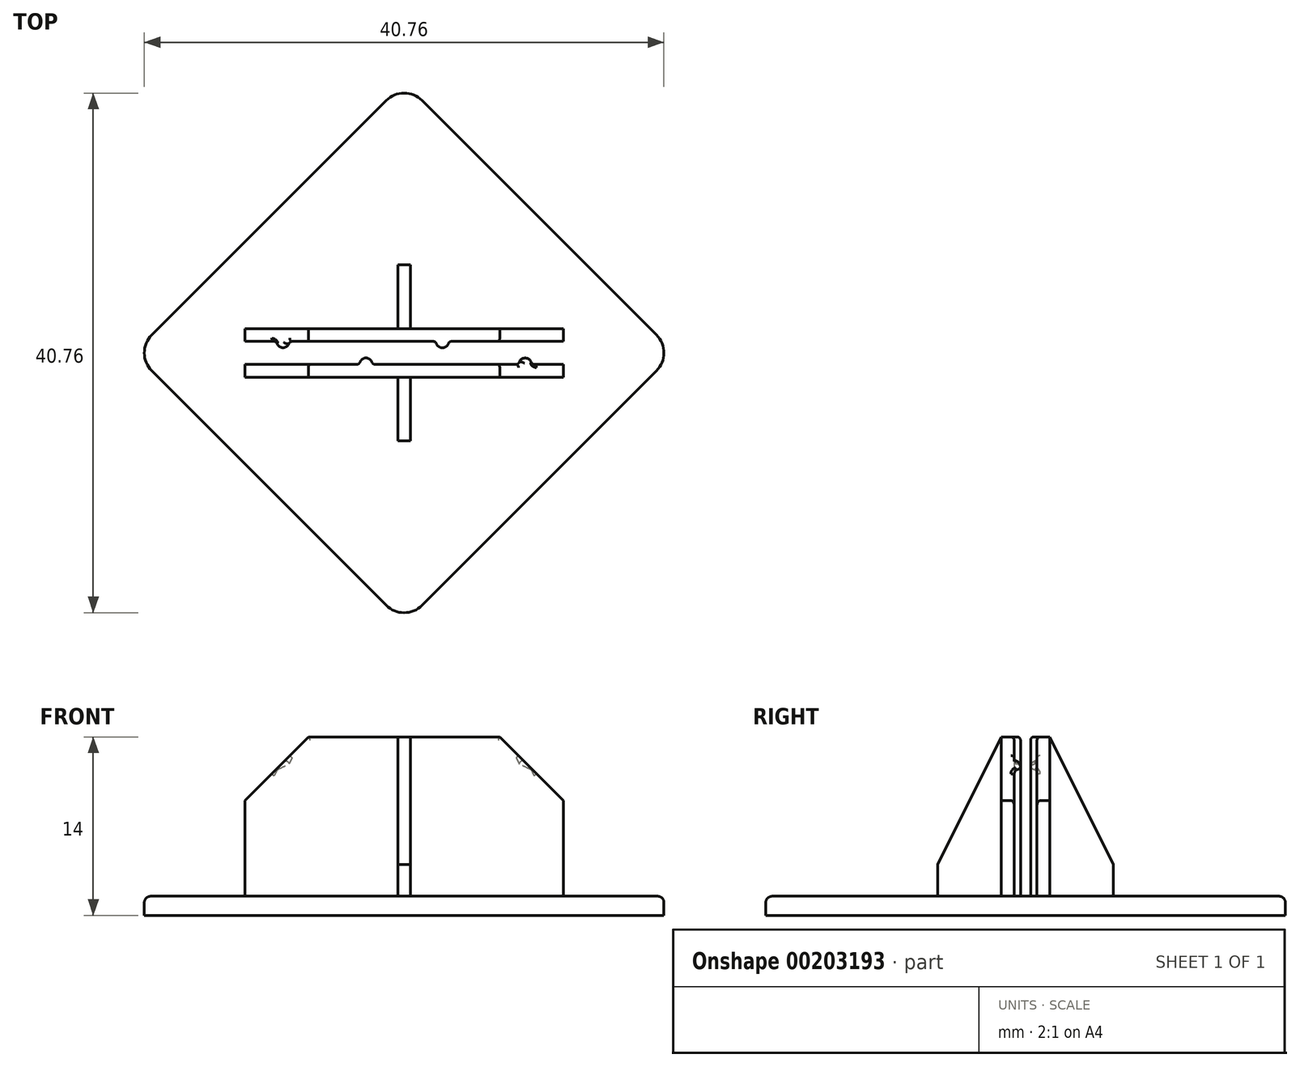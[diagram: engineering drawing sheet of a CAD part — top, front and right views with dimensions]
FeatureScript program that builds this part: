
annotation { "Feature Type Name" : "Feature", "Feature Type Description" : "" }
export const myFeature = defineFeature(function(context is Context, id is Id, definition is map)
    precondition{}
    {
        {
            var Q0;
            Q0=qCreatedBy(makeId("Front.planeOp"),FACE);
            var sketch = newSketch(context, id + "F0", { "sketchPlane" : qUnion([Q0])});
            skLineSegment(sketch, "E0", {"start": v(0, 0) * mm, "end": v(0, 22.97) * mm, "construction": true});
            skSolve(sketch);
        }
        {
            var Q0;
            Q0=qCreatedBy(makeId("Top.planeOp"),FACE);
            var sketch = newSketch(context, id + "F1", { "sketchPlane" : qUnion([Q0])});
            skLineSegment(sketch, "E1.bottom", {"start": v(15, -15) * mm, "end": v(-15, -15) * mm});
            skLineSegment(sketch, "E1.top", {"start": v(15, 15) * mm, "end": v(-15, 15) * mm});
            skLineSegment(sketch, "E1.left", {"start": v(15, -15) * mm, "end": v(15, 15) * mm});
            skLineSegment(sketch, "E1.right", {"start": v(-15, -15) * mm, "end": v(-15, 15) * mm});
            skPoint(sketch, "E1.middle", {"position": v(0, 0) * mm});
            skSolve(sketch);
        }
        {
            var Q0;
            Q0=makeQuery(id+"F1.imprint","IMPRINT",FACE,{"disambiguationData":[TD([[makeQuery(id+"F1.imprint","IMPRINT",EDGE,{"derivedFrom":sQuery(id+"F1.wireOp",EDGE,"E1.bottom")}),-1.0]])]});
            extrude(context, id + "F2", {"entities" : qUnion([Q0]), "depth" : 1.5 * mm});
        }
        {
            var Q0;
            Q0=makeQuery(id+"F2.opExtrude","SWEPT_BODY",BODY,{"disambiguationData":[OSD([sQuery(id+"F1.wireOp",EDGE,"E1.bottom"),sQuery(id+"F1.wireOp",EDGE,"E1.top"),sQuery(id+"F1.wireOp",EDGE,"E1.left"),sQuery(id+"F1.wireOp",EDGE,"E1.right")])]});
            var Q1;
            Q1=sQuery(id+"F0.wireOp",EDGE,"E0");
            transform(context, id + "F3", {"entities" : qUnion([Q0]), "transformType" : TransformType.ROTATION, "transformAxis" : qUnion([Q1]), "angle" : 45 * degree, "makeCopy" : false});
        }
        {
            var Q0;
            Q0=makeQuery(id+"F2.opExtrude","SWEPT_EDGE",EDGE,{"disambiguationData":[OSD([sQuery(id+"F1.wireOp",EDGE,"E1.top"),sQuery(id+"F1.wireOp",EDGE,"E1.right")])]});
            var Q1;
            Q1=makeQuery(id+"F2.opExtrude","SWEPT_EDGE",EDGE,{"disambiguationData":[OSD([sQuery(id+"F1.wireOp",EDGE,"E1.bottom"),sQuery(id+"F1.wireOp",EDGE,"E1.right")])]});
            var Q2;
            Q2=makeQuery(id+"F2.opExtrude","SWEPT_EDGE",EDGE,{"disambiguationData":[OSD([sQuery(id+"F1.wireOp",EDGE,"E1.bottom"),sQuery(id+"F1.wireOp",EDGE,"E1.left")])]});
            var Q3;
            Q3=makeQuery(id+"F2.opExtrude","SWEPT_EDGE",EDGE,{"disambiguationData":[OSD([sQuery(id+"F1.wireOp",EDGE,"E1.top"),sQuery(id+"F1.wireOp",EDGE,"E1.left")])]});
            fillet(context, id + "F4", {"entities" : qUnion([Q0, Q1, Q2, Q3]), "radius" : 2 * mm, "tangentPropagation" : true, "allowEdgeOverflow" : false});
        }
        {
            var Q0;
            Q0=makeQuery(id+"F2.opExtrude","CAP_FACE",FACE,{"disambiguationData":[OSD([sQuery(id+"F1.wireOp",EDGE,"E1.bottom"),sQuery(id+"F1.wireOp",EDGE,"E1.top"),sQuery(id+"F1.wireOp",EDGE,"E1.left"),sQuery(id+"F1.wireOp",EDGE,"E1.right")])],"isStart":false});
            fillet(context, id + "F5", {"entities" : qUnion([Q0]), "radius" : .5 * mm, "tangentPropagation" : true, "allowEdgeOverflow" : false});
        }
        {
            var Q0;
            Q0=makeQuery(id+"F2.opExtrude","CAP_FACE",FACE,{"disambiguationData":[OSD([sQuery(id+"F1.wireOp",EDGE,"E1.bottom"),sQuery(id+"F1.wireOp",EDGE,"E1.top"),sQuery(id+"F1.wireOp",EDGE,"E1.left"),sQuery(id+"F1.wireOp",EDGE,"E1.right")])],"isStart":false});
            var sketch = newSketch(context, id + "F6", { "sketchPlane" : qUnion([Q0])});
            skLineSegment(sketch, "E2", {"start": v(-18.38, 0) * mm, "end": v(18.38, 0) * mm, "construction": true});
            skLineSegment(sketch, "E3.0", {"start": v(-18.38, 1) * mm, "end": v(18.38, 1) * mm, "construction": true});
            skLineSegment(sketch, "E4.0", {"start": v(-18.38, 2) * mm, "end": v(18.38, 2) * mm, "construction": true});
            skLineSegment(sketch, "E5.0", {"start": v(-18.38, 7) * mm, "end": v(18.38, 7) * mm, "construction": true});
            skLineSegment(sketch, "E6", {"start": v(0, 18.38) * mm, "end": v(0, -18.38) * mm, "construction": true});
            skLineSegment(sketch, "E7.0", {"start": v(-12.5, 18.38) * mm, "end": v(-12.5, -18.38) * mm, "construction": true});
            skLineSegment(sketch, "E8.0", {"start": v(12.5, 18.38) * mm, "end": v(12.5, -18.38) * mm, "construction": true});
            skLineSegment(sketch, "E9.0", {"start": v(-0.5, 18.38) * mm, "end": v(-0.5, -18.38) * mm, "construction": true});
            skLineSegment(sketch, "E10.0", {"start": v(0.5, 18.38) * mm, "end": v(0.5, -18.38) * mm, "construction": true});
            skLineSegment(sketch, "E11.0", {"start": v(-9.5, 18.38) * mm, "end": v(-9.5, -18.38) * mm, "construction": true});
            skLineSegment(sketch, "E12.0", {"start": v(3, 18.38) * mm, "end": v(3, -18.38) * mm, "construction": true});
            skCircle(sketch, "E13", {"center": v(-9.5, 1) * mm, "radius": 0.5 * mm});
            skCircle(sketch, "E14", {"center": v(3, 1) * mm, "radius": 0.5 * mm});
            skLineSegment(sketch, "E15", {"start": v(0.5, 7) * mm, "end": v(0.5, 2) * mm});
            skLineSegment(sketch, "E16", {"start": v(0.5, 2) * mm, "end": v(12.5, 2) * mm});
            skLineSegment(sketch, "E17", {"start": v(12.5, 2) * mm, "end": v(12.5, 1) * mm});
            skLineSegment(sketch, "E18", {"start": v(12.5, 1) * mm, "end": v(-12.5, 1) * mm});
            skLineSegment(sketch, "E19", {"start": v(-12.5, 1) * mm, "end": v(-12.5, 2) * mm});
            skLineSegment(sketch, "E20", {"start": v(-12.5, 2) * mm, "end": v(-0.5, 2) * mm});
            skLineSegment(sketch, "E21", {"start": v(-0.5, 2) * mm, "end": v(-0.5, 7) * mm});
            skLineSegment(sketch, "E22", {"start": v(-0.5, 7) * mm, "end": v(0.5, 7) * mm});
            skSolve(sketch);
        }
        {
            var Q0;
            Q0=makeQuery(id+"F6.imprint","IMPRINT",FACE,{"disambiguationData":[TD([[makeQuery(id+"F6.imprint","IMPRINT",EDGE,{"derivedFrom":sQuery(id+"F6.wireOp",EDGE,"E15")}),-1.0]])]});
            var Q1;
            {var subQ0=sQuery(id+"F6.wireOp",EDGE,"E18");var subQ1=sQuery(id+"F6.wireOp",EDGE,"E13");var subQ2=makeQuery(id+"F6.imprint","INTERSECT",VERTEX,{"disambiguationData":[OD(0.0)],"derivedFrom":[subQ1,subQ0]});Q1=makeQuery(id+"F6.imprint","IMPRINT",FACE,{"disambiguationData":[TD([[makeQuery(id+"F6.imprint","IMPRINT",EDGE,{"disambiguationData":[TD([[subQ2,-1.0]])],"derivedFrom":subQ1}),1.0]])]});}
            var Q2;
            {var subQ0=sQuery(id+"F6.wireOp",EDGE,"E18");var subQ1=sQuery(id+"F6.wireOp",EDGE,"E13");var subQ2=makeQuery(id+"F6.imprint","INTERSECT",VERTEX,{"disambiguationData":[OD(0.0)],"derivedFrom":[subQ1,subQ0]});Q2=makeQuery(id+"F6.imprint","IMPRINT",FACE,{"disambiguationData":[TD([[makeQuery(id+"F6.imprint","IMPRINT",EDGE,{"disambiguationData":[TD([[subQ2,1.0]])],"derivedFrom":subQ1}),1.0]])]});}
            var Q3;
            {var subQ0=sQuery(id+"F6.wireOp",EDGE,"E18");var subQ1=sQuery(id+"F6.wireOp",EDGE,"E14");var subQ2=makeQuery(id+"F6.imprint","INTERSECT",VERTEX,{"disambiguationData":[OD(0.0)],"derivedFrom":[subQ1,subQ0]});Q3=makeQuery(id+"F6.imprint","IMPRINT",FACE,{"disambiguationData":[TD([[makeQuery(id+"F6.imprint","IMPRINT",EDGE,{"disambiguationData":[TD([[subQ2,-1.0]])],"derivedFrom":subQ1}),1.0]])]});}
            var Q4;
            {var subQ0=sQuery(id+"F6.wireOp",EDGE,"E18");var subQ1=sQuery(id+"F6.wireOp",EDGE,"E14");var subQ2=makeQuery(id+"F6.imprint","INTERSECT",VERTEX,{"disambiguationData":[OD(0.0)],"derivedFrom":[subQ1,subQ0]});Q4=makeQuery(id+"F6.imprint","IMPRINT",FACE,{"disambiguationData":[TD([[makeQuery(id+"F6.imprint","IMPRINT",EDGE,{"disambiguationData":[TD([[subQ2,1.0]])],"derivedFrom":subQ1}),1.0]])]});}
            extrude(context, id + "F7", {"entities" : qUnion([Q0, Q1, Q2, Q3, Q4]), "depth" : 12.5 * mm});
        }
        {
            var Q0;
            Q0=makeQuery(id+"F7.opExtrude","CAP_EDGE",EDGE,{"disambiguationData":[OSD([sQuery(id+"F6.wireOp",EDGE,"E17")])],"isStart":false});
            var Q1;
            Q1=makeQuery(id+"F7.opExtrude","CAP_EDGE",EDGE,{"disambiguationData":[OSD([sQuery(id+"F6.wireOp",EDGE,"E19")])],"isStart":false});
            chamfer(context, id + "F8", {"entities" : qUnion([Q0, Q1]), "width" : 5 * mm, "tangentPropagation" : true});
        }
        {
            var Q0;
            Q0=makeQuery(id+"F7.opExtrude","CAP_EDGE",EDGE,{"disambiguationData":[OSD([sQuery(id+"F6.wireOp",EDGE,"E22")])],"isStart":false});
            chamfer(context, id + "F9", {"entities" : qUnion([Q0]), "chamferType" : ChamferType.TWO_OFFSETS, "width1" : 10 * mm, "oppositeDirection" : false, "width2" : 5 * mm, "tangentPropagation" : true});
        }
        {
            var Q0;
            {var subQ0=sQuery(id+"F6.wireOp",EDGE,"E18");var subQ1=sQuery(id+"F6.wireOp",EDGE,"E14");Q0=makeQuery(id+"F7.opExtrude","SWEPT_EDGE",EDGE,{"disambiguationData":[OSD([subQ1,subQ0]),TDD([makeQuery(id+"F6.imprint","INTERSECT",VERTEX,{"disambiguationData":[OD(0.0)],"derivedFrom":[subQ1,subQ0]})])]});}
            var Q1;
            {var subQ0=sQuery(id+"F6.wireOp",EDGE,"E18");var subQ1=sQuery(id+"F6.wireOp",EDGE,"E13");Q1=makeQuery(id+"F7.opExtrude","SWEPT_EDGE",EDGE,{"disambiguationData":[OSD([subQ1,subQ0]),TDD([makeQuery(id+"F6.imprint","INTERSECT",VERTEX,{"disambiguationData":[OD(0.0)],"derivedFrom":[subQ1,subQ0]})])]});}
            var Q2;
            {var subQ0=sQuery(id+"F6.wireOp",EDGE,"E18");var subQ1=sQuery(id+"F6.wireOp",EDGE,"E14");Q2=makeQuery(id+"F7.opExtrude","SWEPT_EDGE",EDGE,{"disambiguationData":[OSD([subQ1,subQ0]),TDD([makeQuery(id+"F6.imprint","INTERSECT",VERTEX,{"disambiguationData":[OD(1.0)],"derivedFrom":[subQ1,subQ0]})])]});}
            var Q3;
            {var subQ0=sQuery(id+"F6.wireOp",EDGE,"E18");var subQ1=sQuery(id+"F6.wireOp",EDGE,"E13");Q3=makeQuery(id+"F7.opExtrude","SWEPT_EDGE",EDGE,{"disambiguationData":[OSD([subQ1,subQ0]),TDD([makeQuery(id+"F6.imprint","INTERSECT",VERTEX,{"disambiguationData":[OD(1.0)],"derivedFrom":[subQ1,subQ0]})])]});}
            fillet(context, id + "F10", {"entities" : qUnion([Q0, Q1, Q2, Q3]), "radius" : .25 * mm, "tangentPropagation" : true, "allowEdgeOverflow" : false});
        }
        {
            var Q0;
            {var subQ0=sQuery(id+"F6.wireOp",EDGE,"E19");var subQ1=sQuery(id+"F6.wireOp",EDGE,"E18");Q0=makeQuery(id+"F8.opChamfer","BLEND_EDGE",EDGE,{"blendedFrom":[makeQuery(id+"F7.opExtrude","CAP_EDGE",EDGE,{"disambiguationData":[OSD([subQ0])],"isStart":false}),makeQuery(id+"F7.opExtrude","SWEPT_FACE",FACE,{"disambiguationData":[OSD([subQ1]),TDD([makeQuery(id+"F6.imprint","IMPRINT",EDGE,{"disambiguationData":[TD([[makeQuery(id+"F6.imprint","INTERSECT",VERTEX,{"derivedFrom":[subQ1,subQ0]}),1.0]])],"derivedFrom":subQ1})])]})],"blendedInto":[makeQuery(id+"F7.opExtrude","SWEPT_FACE",FACE,{"disambiguationData":[OSD([subQ1]),TDD([makeQuery(id+"F6.imprint","IMPRINT",EDGE,{"disambiguationData":[TD([[makeQuery(id+"F6.imprint","INTERSECT",VERTEX,{"derivedFrom":[subQ1,subQ0]}),1.0]])],"derivedFrom":subQ1})])]})]});}
            var Q1;
            {var subQ0=sQuery(id+"F6.wireOp",EDGE,"E18");Q1=makeQuery(id+"F7.opExtrude","CAP_EDGE",EDGE,{"disambiguationData":[OSD([subQ0]),TDD([makeQuery(id+"F6.imprint","IMPRINT",EDGE,{"disambiguationData":[TD([[makeQuery(id+"F6.imprint","INTERSECT",VERTEX,{"disambiguationData":[OD(0.0)],"derivedFrom":[sQuery(id+"F6.wireOp",EDGE,"E13"),subQ0]}),1.0]])],"derivedFrom":subQ0})])],"isStart":false});}
            var Q2;
            {var subQ0=sQuery(id+"F6.wireOp",EDGE,"E18");var subQ1=sQuery(id+"F6.wireOp",EDGE,"E17");Q2=makeQuery(id+"F8.opChamfer","BLEND_EDGE",EDGE,{"blendedFrom":[makeQuery(id+"F7.opExtrude","CAP_EDGE",EDGE,{"disambiguationData":[OSD([subQ1])],"isStart":false}),makeQuery(id+"F7.opExtrude","SWEPT_FACE",FACE,{"disambiguationData":[OSD([subQ0]),TDD([makeQuery(id+"F6.imprint","IMPRINT",EDGE,{"disambiguationData":[TD([[makeQuery(id+"F6.imprint","INTERSECT",VERTEX,{"derivedFrom":[subQ1,subQ0]}),-1.0]])],"derivedFrom":subQ0})])]})],"blendedInto":[makeQuery(id+"F7.opExtrude","SWEPT_FACE",FACE,{"disambiguationData":[OSD([subQ0]),TDD([makeQuery(id+"F6.imprint","IMPRINT",EDGE,{"disambiguationData":[TD([[makeQuery(id+"F6.imprint","INTERSECT",VERTEX,{"derivedFrom":[subQ1,subQ0]}),-1.0]])],"derivedFrom":subQ0})])]})]});}
            fillet(context, id + "F11", {"entities" : qUnion([Q0, Q1, Q2]), "radius" : .25 * mm, "tangentPropagation" : true, "allowEdgeOverflow" : false});
        }
        {
            var Q0;
            Q0=makeQuery(id+"F7.opExtrude","SWEPT_BODY",BODY,{"disambiguationData":[OSD([sQuery(id+"F6.wireOp",EDGE,"E13"),sQuery(id+"F6.wireOp",EDGE,"E14"),sQuery(id+"F6.wireOp",EDGE,"E15"),sQuery(id+"F6.wireOp",EDGE,"E16"),sQuery(id+"F6.wireOp",EDGE,"E17"),sQuery(id+"F6.wireOp",EDGE,"E18"),sQuery(id+"F6.wireOp",EDGE,"E19"),sQuery(id+"F6.wireOp",EDGE,"E20"),sQuery(id+"F6.wireOp",EDGE,"E21"),sQuery(id+"F6.wireOp",EDGE,"E22")])]});
            var Q1;
            Q1=sQuery(id+"F0.wireOp",EDGE,"E0");
            transform(context, id + "F12", {"entities" : qUnion([Q0]), "transformType" : TransformType.ROTATION, "transformAxis" : qUnion([Q1]), "angle" : 180 * degree, "makeCopy" : true});
        }
        {
            var Q0;
            Q0=makeQuery(id+"F7.opExtrude","SWEPT_BODY",BODY,{"disambiguationData":[OSD([sQuery(id+"F6.wireOp",EDGE,"E13"),sQuery(id+"F6.wireOp",EDGE,"E14"),sQuery(id+"F6.wireOp",EDGE,"E15"),sQuery(id+"F6.wireOp",EDGE,"E16"),sQuery(id+"F6.wireOp",EDGE,"E17"),sQuery(id+"F6.wireOp",EDGE,"E18"),sQuery(id+"F6.wireOp",EDGE,"E19"),sQuery(id+"F6.wireOp",EDGE,"E20"),sQuery(id+"F6.wireOp",EDGE,"E21"),sQuery(id+"F6.wireOp",EDGE,"E22")])]});
            transform(context, id + "F13", {"entities" : qUnion([Q0]), "transformType" : TransformType.TRANSLATION_3D, "dx" : 0 * mm, "dy" : -.1 * mm, "dz" : 0 * mm, "makeCopy" : false});
        }
        {
            var Q0;
            Q0=makeQuery(id+"F12.opPattern","COPY",BODY,{"derivedFrom":makeQuery(id+"F7.opExtrude","SWEPT_BODY",BODY,{"disambiguationData":[OSD([sQuery(id+"F6.wireOp",EDGE,"E13"),sQuery(id+"F6.wireOp",EDGE,"E14"),sQuery(id+"F6.wireOp",EDGE,"E15"),sQuery(id+"F6.wireOp",EDGE,"E16"),sQuery(id+"F6.wireOp",EDGE,"E17"),sQuery(id+"F6.wireOp",EDGE,"E18"),sQuery(id+"F6.wireOp",EDGE,"E19"),sQuery(id+"F6.wireOp",EDGE,"E20"),sQuery(id+"F6.wireOp",EDGE,"E21"),sQuery(id+"F6.wireOp",EDGE,"E22")])]}),"instanceName":"1"});
            transform(context, id + "F14", {"entities" : qUnion([Q0]), "transformType" : TransformType.TRANSLATION_3D, "dx" : 0 * mm, "dy" : .1 * mm, "dz" : 0 * mm, "makeCopy" : false});
        }
    });
